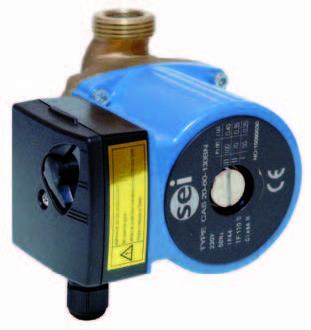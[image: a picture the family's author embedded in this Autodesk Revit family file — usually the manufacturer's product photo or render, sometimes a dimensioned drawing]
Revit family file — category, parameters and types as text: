
# Revit family: CAS_20-60BN-AC52152
name_source: partatom
category: Aparatos eléctricos
revit_build: Autodesk Revit 2016 (Build: 20150220_1215(x64)
units: mm (PartAtom-declared; Revit-internal decimal feet)

## family parameters
Compartido = No
Corte con vacíos al cargar = No
Cota de conector redondo = Diámetro de uso
Mantener orientación de anotación = No
Número OmniClass = 23.80.00.00
Punto de cálculo de habitación = No
Se basa en plano de trabajo = No
Siempre vertical = Sí
Tipo de pieza = Caja de conexiones
Título OmniClass = Electric Power and Lighting

## types (2) — shared parameters
Fabricante = SALVADOR ESCODA
URL = www.salvadorescoda.com
zero-valued in all types: Costo

## per-type parameters (varying)
| type | Aislamiento | Caudal | Conexión racores | Código de montaje | Descripción | Dimensiones Unidad Interior | Imagen de tipo | Intensidad máx | Modelo | Motor | Máx. presión trabajo | Peso | Potencia máx | Presión disponible | Protección | Rango temperatura agua | Regulable | Temperatura ambiente |
| MVD-22T2 | 35 dB(A) |  |  | CL23370 | CONDUCTO BAJA SILUETA | 700 x 210 x 500 mm | <Ninguno> |  | MVD-22T2/DHN1-DA5 | 521 m3/h | 2,2kW / 39W | 17,5 kg neto |  |  | 6,35 mm (1/4") | 2,6kW / 39W |  | DC / WZDK100-38GS |
| CAS | Clase H | 1,5 m3/h | 1" DN | AC52152 | BOMBA CIRCULADORA PARA ACS | 130 x 130 x 130 mm | SEI_CAS.jpg | 0,45 A | CAS 20-60 BN | 2 polos, 1x230V - 50Hz | 10 bar | 2,9 Kgs | 100 W | 4 m.c.a. | IP 44 | 2º a 110 ºC | 3 velocidades | Hasta 40ºC |
